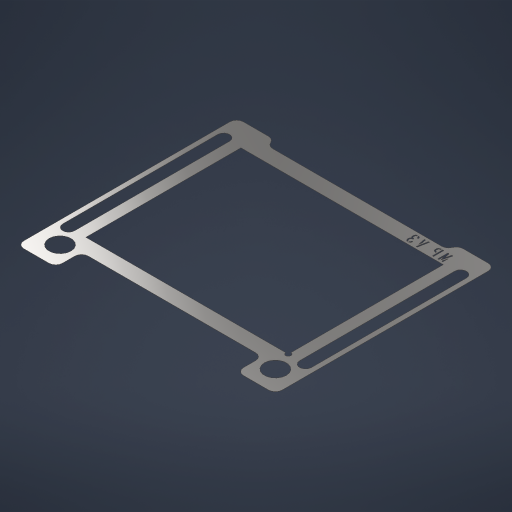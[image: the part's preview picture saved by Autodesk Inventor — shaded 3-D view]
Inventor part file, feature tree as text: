
AUTODESK INVENTOR PART (.ipt)
format: ipt  version: 2024 (Build 280153000, 153)  size: 449,536 bytes
history: native  units: in
note: dims shown in document units (in); Inventor stores cm internally (conversion verified against a paired STEP export)
features: extrude x5, sketch x3, hole x1, fillet x1, emboss x1
ambient origin geometry x8: Origin, YZ Plane, XZ Plane, XY Plane, X Axis, Y Axis, Z Axis, Center Point
bodies: Solid1 (feature_tree)
feature tree (11):
  extrude  "Extrusion1"  Depth=2.75in
  extrude  "Extrusion2"  Depth=0.1378in
  extrude  "Extrusion3"  Depth=1.8in
  hole  "Hole1"  [1 undecoded]
  extrude  "Extrusion4"  Depth=0.3in
  extrude  "Extrusion5"  Depth=2.1in
  fillet  "Fillet1"  Radius=0.45in
  emboss  "Emboss2"
  sketch  "Sketch2"  dims[d0=3.0in d1=2.75in]
  sketch  "Sketch3"  dims[d2=0.002in d3=0.0in d4=0.1378in]
  sketch  "Sketch8"  dims[d5=0.125in d6=1.8in d7=0.0in d8=0.0in d9=0.3in d10=2.1in d11=0.45in d12=0.0in d13=0.0in d14=0.25in d15=0.25in d16=0.25in d17=0.25in d18=0.25in d19=0.25in d20=0.25in d21=0.25in d22=0.255in d23=0.75in d24=0.156in d25=0.073in d26=0.5635in d27=1.0in d28=0.8108in d29=0.2in d30=0.0in d31=0.0in d32=0.0625in d33=1.8in d34=2.35in d35=0.0in d36=0.0in d37=0.0787in d38=0.225in d39=0.075in d42=0.0394in d43=0.0in]
note: 1 required parameter value undecoded (feature->parameter linkage not recoverable at this tier; creation-order binding heuristic only, values carry confidence <= 0.55)
